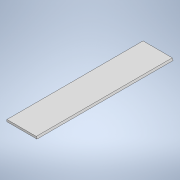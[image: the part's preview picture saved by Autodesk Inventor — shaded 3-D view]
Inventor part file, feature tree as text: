
AUTODESK INVENTOR PART (.ipt)
format: ipt  version: 2021 (Build 250183000, 183)  size: 101,376 bytes
history: native  units: in
note: dims shown in document units (in); Inventor stores cm internally (conversion verified against a paired STEP export)
features: extrude x2, sketch x2
ambient origin geometry x8: Origin, YZ Plane, XZ Plane, XY Plane, X Axis, Y Axis, Z Axis, Center Point
bodies: Solid1 (feature_tree)
feature tree (4):
  extrude  "Extrusion1"  Depth=6.8in
  extrude  "Extrusion2"  Depth=6.8in
  sketch  "Sketch1"  dims[d0=1.5in d1=6.8in]
  sketch  "Sketch2"  dims[d2=0.1in d3=0.0in d4=0.1374in d5=6.8in d6=0.0in]
